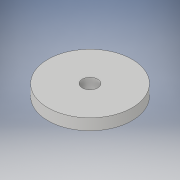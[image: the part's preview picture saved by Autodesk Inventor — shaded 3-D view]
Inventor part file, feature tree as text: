
AUTODESK INVENTOR PART (.ipt)
format: ipt  version: 2018 (Build 220112000, 112)  size: 97,792 bytes
history: native  units: in
note: dims shown in document units (in); Inventor stores cm internally (conversion verified against a paired STEP export)
features: sketch x2, extrude x1, hole x1
ambient origin geometry x8: Origin, YZ Plane, XZ Plane, XY Plane, X Axis, Y Axis, Z Axis, Center Point
bodies: Solid1 (feature_tree)
feature tree (4):
  extrude  "Extrusion1"  Depth=0.08in TaperAngle=0.0deg
  hole  "Hole1"  [1 undecoded]
  sketch  "Sketch1"  dims[d0=0.6in d1=0.08in d2=0.0in]
  sketch  "Sketch2"  dims[d3=0.11in d4=0.11in d5=0.75in d6=0.375in d7=0.25in d8=0.5635in d9=1.0in d10=0.8108in]
note: 1 required parameter value undecoded (feature->parameter linkage not recoverable at this tier; creation-order binding heuristic only, values carry confidence <= 0.55)
